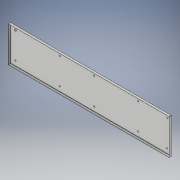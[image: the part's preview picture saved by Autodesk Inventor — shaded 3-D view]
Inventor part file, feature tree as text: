
AUTODESK INVENTOR PART (.ipt)
format: ipt  version: 2018 (Build 220112000, 112)  size: 258,560 bytes
history: native  units: in
note: dims shown in document units (in); Inventor stores cm internally (conversion verified against a paired STEP export)
features: sketch x4, sheet_metal_op x4, other x2, extrude x1
ambient origin geometry x8: Origin, YZ Plane, XZ Plane, XY Plane, X Axis, Y Axis, Z Axis, Center Point
bodies: Solid1 (feature_tree)
feature tree (11):
  sketch  "Sketch1"  dims[d0=0.25in d1=0.25in]
  sheet_metal_op  "Face1"
  extrude  "Extrusion1"  Depth=0.25in
  sheet_metal_op  "Flange1"
  sketch  "Sketch2"  dims[d2=0.25in]
  other  "Plate1"
  sketch  "Sketch3"  dims[d3=0.25in]
  sketch  "Sketch4"  dims[d4=0.0197in d5=0.187in d6=0.0in d7=0.0in d8=0.0197in d9=0.0098in d10=0.0394in d11=0.0197in d12=0.315in d13=90.0deg d14=0.0197in d15=0.0787in d16=0.0197in d17=0.0197in]
  other  "Plate2"
  sheet_metal_op  "Bend1"
  sheet_metal_op  "Corner1"
